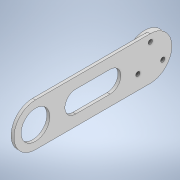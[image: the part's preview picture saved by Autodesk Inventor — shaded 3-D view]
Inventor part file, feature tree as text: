
AUTODESK INVENTOR PART (.ipt)
format: ipt  version: 2022 (Build 260153000, 153)  size: 131,584 bytes
history: native  units: mm
features: extrude x2, sketch x1
ambient origin geometry x8: Origin, YZ Plane, XZ Plane, XY Plane, X Axis, Y Axis, Z Axis, Center Point
bodies: Solid1 (feature_tree)
feature tree (3):
  sketch  "Sketch1"  dims[d0=30.0mm d1=80.0mm d2=20.0mm d3=2.0mm d4=0.0mm d5=15.0mm d6=3.0mm d7=30.0mm d9=360.0deg d11=2.0mm d12=0.0mm d13=24.0mm]
  extrude  "Extrusion1"  Depth=2.0mm
  extrude  "Extrusion2"  Depth=2.0mm
